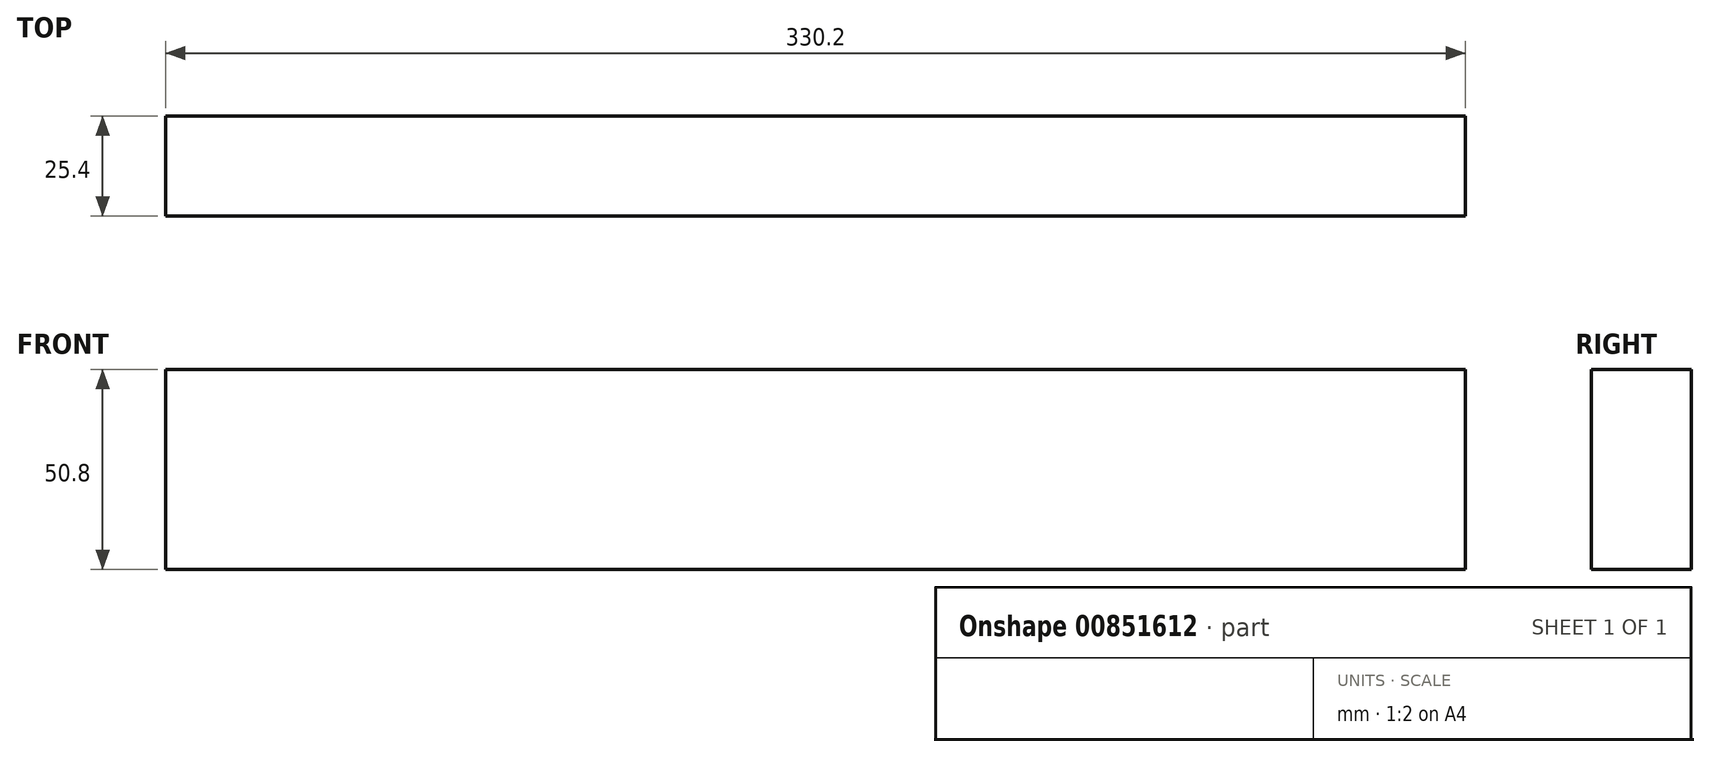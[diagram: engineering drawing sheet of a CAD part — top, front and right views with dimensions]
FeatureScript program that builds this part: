
annotation { "Feature Type Name" : "Feature", "Feature Type Description" : "" }
export const myFeature = defineFeature(function(context is Context, id is Id, definition is map)
    precondition{}
    {
        {
            var Q0;
            Q0=qCreatedBy(makeId("Front.planeOp"),FACE);
            var sketch = newSketch(context, id + "F0", { "sketchPlane" : qUnion([Q0])});
            skLineSegment(sketch, "E0", {"start": v(-65.52, -17.93) * mm, "end": v(-65.52, -68.73) * mm});
            skLineSegment(sketch, "E1", {"start": v(-65.52, -17.93) * mm, "end": v(264.68, -17.93) * mm});
            skLineSegment(sketch, "E2", {"start": v(-65.52, -68.73) * mm, "end": v(264.68, -68.73) * mm});
            skLineSegment(sketch, "E3", {"start": v(264.68, -68.73) * mm, "end": v(264.68, -17.93) * mm});
            skSolve(sketch);
        }
        {
            var Q0;
            Q0 = qSketchRegion(id + "F0", true);
            extrude(context, id + "F1", {"entities" : qUnion([Q0]), "depth" : 25.4 * mm, "offsetDistance" : 25.4 * mm});
        }
    });
